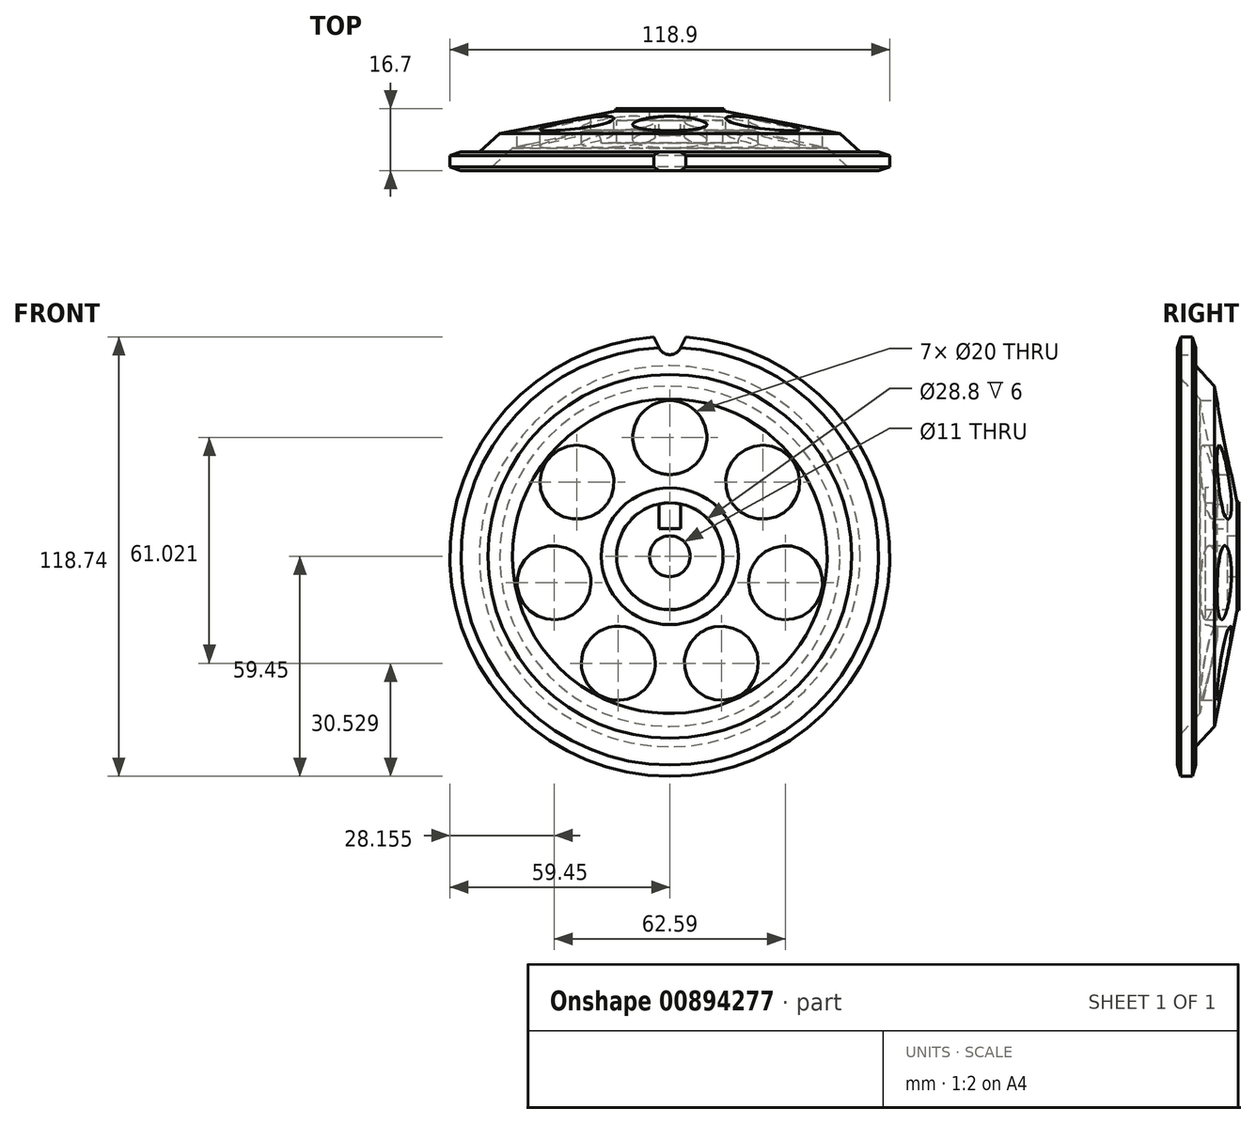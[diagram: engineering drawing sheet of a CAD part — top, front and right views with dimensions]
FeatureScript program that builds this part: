
annotation { "Feature Type Name" : "Feature", "Feature Type Description" : "" }
export const myFeature = defineFeature(function(context is Context, id is Id, definition is map)
    precondition{}
    {
        {
            var Q0;
            Q0=qCreatedBy(makeId("Right.planeOp"),FACE);
            var sketch = newSketch(context, id + "F0", { "sketchPlane" : qUnion([Q0])});
            skLineSegment(sketch, "E0.MirrorCS", {"start": v(-3.2, 5.5) * mm, "end": v(0, 5.5) * mm});
            skLineSegment(sketch, "E1.MirrorCS", {"start": v(0, 14.65) * mm, "end": v(-0.6, 14.65) * mm});
            skLineSegment(sketch, "E2.MirrorCS", {"start": v(-12.65, 59.45) * mm, "end": v(-15.75, 59.45) * mm});
            skLineSegment(sketch, "E3.MirrorCS", {"start": v(-11.7, 56.45) * mm, "end": v(-12.65, 59.45) * mm});
            skLineSegment(sketch, "E4.MirrorCS", {"start": v(-15.75, 59.45) * mm, "end": v(-16.7, 56.45) * mm});
            skLineSegment(sketch, "E5.MirrorCS", {"start": v(-9.2, 18.5) * mm, "end": v(-9.2, 14.4) * mm});
            skLineSegment(sketch, "E6.MirrorCS", {"start": v(0, 0) * mm, "end": v(-34.56, 0) * mm, "construction": true});
            skArc(sketch, "E7.MirrorCS", {"start": v(-5.95, 22.6) * mm, "mid": v(-6.59, 19.76) * mm, "end": v(-9.2, 18.5) * mm});
            skLineSegment(sketch, "E8.MirrorCS", {"start": v(-9.2, 14.4) * mm, "end": v(-3.2, 14.4) * mm});
            skLineSegment(sketch, "E9.MirrorCS", {"start": v(-3.2, 14.4) * mm, "end": v(-3.2, 5.5) * mm});
            skLineSegment(sketch, "E10.MirrorCS", {"start": v(0, 0) * mm, "end": v(0, 5.5) * mm, "construction": true});
            skLineSegment(sketch, "E11.MirrorCS", {"start": v(-0.6, 14.65) * mm, "end": v(-6.7, 46) * mm});
            skLineSegment(sketch, "E12.MirrorCS", {"start": v(0, 5.5) * mm, "end": v(0, 14.65) * mm});
            skLineSegment(sketch, "E13.MirrorCS", {"start": v(-6.7, 46) * mm, "end": v(-11.7, 51.5) * mm});
            skLineSegment(sketch, "E14.MirrorCS", {"start": v(-11.7, 51.5) * mm, "end": v(-11.7, 56.45) * mm});
            skLineSegment(sketch, "E15.MirrorCS", {"start": v(-16.7, 56.45) * mm, "end": v(-16.7, 49.17) * mm});
            skLineSegment(sketch, "E16.MirrorCS", {"start": v(-16.7, 49.17) * mm, "end": v(-10.6, 42.5) * mm});
            skLineSegment(sketch, "E17.MirrorCS", {"start": v(-10.6, 42.5) * mm, "end": v(-5.95, 22.6) * mm});
            skLineSegment(sketch, "E18", {"start": v(-9.2, 18.5) * mm, "end": v(-10.48, 18.5) * mm, "construction": true});
            skSolve(sketch);
        }
        {
            var Q0;
            Q0 = qSketchRegion(id + "F0", true);
            var Q1;
            Q1=sQuery(id+"F0.wireOp",EDGE,"E6.MirrorCS");
            revolve(context, id + "F1", {"surfaceOperationType" : NewSurfaceOperationType.NEW, "entities" : qUnion([Q0]), "axis" : qUnion([Q1]), "revolveType" : RevolveType.FULL});
        }
        {
            var Q0;
            Q0=qCreatedBy(makeId("Front.planeOp"),FACE);
            var sketch = newSketch(context, id + "F2", { "sketchPlane" : qUnion([Q0])});
            skCircle(sketch, "E19", {"center": v(0, 32.1) * mm, "radius": 10 * mm});
            skCircle(sketch, "E20.1.0", {"center": v(-25.1, 20.01) * mm, "radius": 10 * mm});
            skCircle(sketch, "E20.2.0", {"center": v(-31.3, -7.14) * mm, "radius": 10 * mm});
            skCircle(sketch, "E20.3.0", {"center": v(-13.93, -28.92) * mm, "radius": 10 * mm});
            skCircle(sketch, "E20.4.0", {"center": v(13.93, -28.92) * mm, "radius": 10 * mm});
            skCircle(sketch, "E20.5.0", {"center": v(31.3, -7.14) * mm, "radius": 10 * mm});
            skCircle(sketch, "E20.6.0", {"center": v(25.1, 20.01) * mm, "radius": 10 * mm});
            skPoint(sketch, "E20.center", {"position": v(0, 0) * mm});
            skSolve(sketch);
        }
        {
            var Q0;
            Q0 = qSketchRegion(id + "F2", true);
            extrude(context, id + "F3", {"entities" : qUnion([Q0]), "operationType" : NewBodyOperationType.REMOVE, "endBound" : BoundingType.THROUGH_ALL, "depth" : 25 * mm, "offsetDistance" : 25 * mm});
        }
        {
            var Q0;
            Q0=makeQuery(id+"F1.opRevolve","SWEPT_FACE",FACE,{"disambiguationData":[OSD([sQuery(id+"F0.wireOp",EDGE,"E9.MirrorCS")])]});
            var sketch = newSketch(context, id + "F4", { "sketchPlane" : qUnion([Q0])});
            skLineSegment(sketch, "E21.bottom", {"start": v(-2.95, 15.5) * mm, "end": v(2.95, 15.5) * mm});
            skLineSegment(sketch, "E21.top", {"start": v(-2.95, 7.5) * mm, "end": v(2.95, 7.5) * mm});
            skLineSegment(sketch, "E21.left", {"start": v(-2.95, 15.5) * mm, "end": v(-2.95, 7.5) * mm});
            skLineSegment(sketch, "E21.right", {"start": v(2.95, 15.5) * mm, "end": v(2.95, 7.5) * mm});
            skLineSegment(sketch, "E22", {"start": v(0, 0) * mm, "end": v(0, 7.5) * mm, "construction": true});
            skSolve(sketch);
        }
        {
            var Q0;
            Q0 = qSketchRegion(id + "F4", true);
            extrude(context, id + "F5", {"entities" : qUnion([Q0]), "operationType" : NewBodyOperationType.ADD, "depth" : 4 * mm, "offsetDistance" : 25 * mm});
        }
        {
            var Q0;
            Q0=makeQuery(id+"F1.opRevolve","SWEPT_FACE",FACE,{"disambiguationData":[OSD([sQuery(id+"F0.wireOp",EDGE,"E14.MirrorCS")])]});
            var sketch = newSketch(context, id + "F6", { "sketchPlane" : qUnion([Q0])});
            skLineSegment(sketch, "E23", {"start": v(-2.87, 56.29) * mm, "end": v(-4.35, 59.3) * mm});
            skLineSegment(sketch, "E24", {"start": v(2.87, 56.29) * mm, "end": v(4.35, 59.3) * mm});
            skArc(sketch, "E25", {"start": v(-2.87, 56.29) * mm, "mid": v(0, 54.5) * mm, "end": v(2.87, 56.29) * mm});
            skLineSegment(sketch, "E26", {"start": v(0, 57.7) * mm, "end": v(0, 0) * mm, "construction": true});
            skArc(sketch, "E27", {"start": v(4.35, 59.3) * mm, "mid": v(0, 59.45) * mm, "end": v(-4.35, 59.3) * mm});
            skSolve(sketch);
        }
        {
            var Q0;
            Q0 = qSketchRegion(id + "F6", true);
            extrude(context, id + "F7", {"entities" : qUnion([Q0]), "operationType" : NewBodyOperationType.REMOVE, "endBound" : BoundingType.THROUGH_ALL, "oppositeDirection" : true, "depth" : 25 * mm, "offsetDistance" : 25 * mm});
        }
    });
